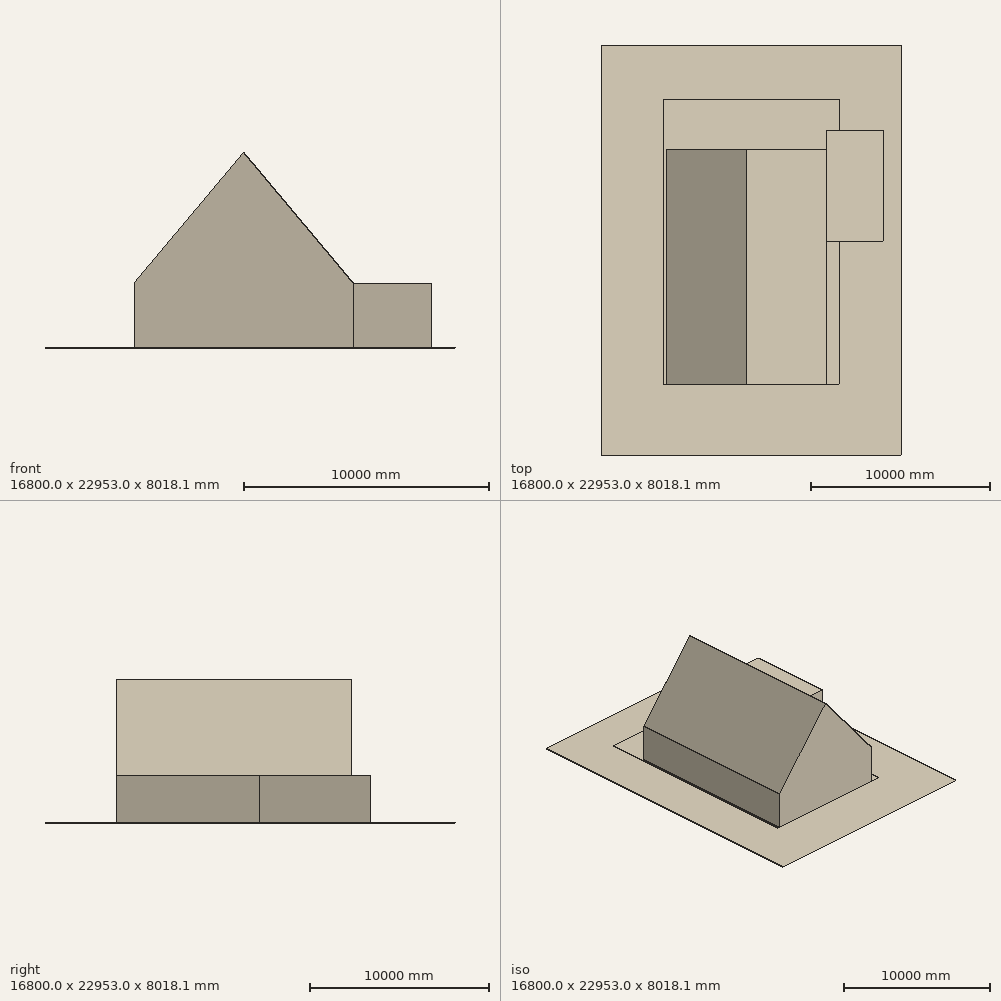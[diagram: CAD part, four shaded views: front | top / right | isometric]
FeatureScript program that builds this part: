
annotation { "Feature Type Name" : "Feature", "Feature Type Description" : "" }
export const myFeature = defineFeature(function(context is Context, id is Id, definition is map)
    precondition{}
    {
        {
            var Q0;
            Q0=qCreatedBy(makeId("Top.planeOp"),FACE);
            var sketch = newSketch(context, id + "F0", { "sketchPlane" : qUnion([Q0])});
            skLineSegment(sketch, "E0.bottom", {"start": v(-5071.58, -11461.11) * mm, "end": v(11728.42, -11461.11) * mm});
            skLineSegment(sketch, "E0.top", {"start": v(-5071.58, 11491.89) * mm, "end": v(11728.42, 11491.89) * mm});
            skLineSegment(sketch, "E0.left", {"start": v(-5071.58, -11461.11) * mm, "end": v(-5071.58, 11491.89) * mm});
            skLineSegment(sketch, "E0.right", {"start": v(11728.42, -11461.11) * mm, "end": v(11728.42, 11491.89) * mm});
            skSolve(sketch);
        }
        {
            var Q0;
            Q0=makeQuery(id+"F0.imprint","IMPRINT",FACE,{"disambiguationData":[TD([[makeQuery(id+"F0.imprint","IMPRINT",EDGE,{"derivedFrom":sQuery(id+"F0.wireOp",EDGE,"E0.bottom")}),1.0]])]});
            extrude(context, id + "F1", {"entities" : qUnion([Q0]), "depth" : 25 * mm, "offsetDistance" : 25 * mm});
        }
        {
            var Q0;
            Q0=makeQuery(id+"F1.opExtrude","CAP_FACE",FACE,{"disambiguationData":[OSD([sQuery(id+"F0.wireOp",EDGE,"E0.bottom"),sQuery(id+"F0.wireOp",EDGE,"E0.top"),sQuery(id+"F0.wireOp",EDGE,"E0.left"),sQuery(id+"F0.wireOp",EDGE,"E0.right")])],"isStart":false});
            var sketch = newSketch(context, id + "F2", { "sketchPlane" : qUnion([Q0])});
            skLineSegment(sketch, "E1.bottom", {"start": v(-1571.58, 8491.89) * mm, "end": v(8228.42, 8491.89) * mm});
            skLineSegment(sketch, "E1.top", {"start": v(-1571.58, -7461.11) * mm, "end": v(8228.42, -7461.11) * mm});
            skLineSegment(sketch, "E1.left", {"start": v(-1571.58, 8491.89) * mm, "end": v(-1571.58, -7461.11) * mm});
            skLineSegment(sketch, "E1.right", {"start": v(8228.42, 8491.89) * mm, "end": v(8228.42, -7461.11) * mm});
            skSolve(sketch);
        }
        {
            var Q0;
            Q0=qSketchRegion(id+"F2",true);
            extrude(context, id + "F3", {"entities" : qUnion([Q0]), "operationType" : NewBodyOperationType.ADD, "depth" : 10 * mm, "offsetDistance" : 25 * mm});
        }
        {
            var Q0;
            Q0=makeQuery(id+"F1.opExtrude","CAP_FACE",FACE,{"disambiguationData":[OSD([sQuery(id+"F0.wireOp",EDGE,"E0.bottom"),sQuery(id+"F0.wireOp",EDGE,"E0.top"),sQuery(id+"F0.wireOp",EDGE,"E0.left"),sQuery(id+"F0.wireOp",EDGE,"E0.right")])],"isStart":false});
            var sketch = newSketch(context, id + "F4", { "sketchPlane" : qUnion([Q0])});
            skLineSegment(sketch, "E2.bottom", {"start": v(-1571.58, 8491.89) * mm, "end": v(-4071.58, 8491.89) * mm});
            skLineSegment(sketch, "E2.top", {"start": v(-1571.58, -6461.11) * mm, "end": v(-4071.58, -6461.11) * mm});
            skLineSegment(sketch, "E2.left", {"start": v(-1571.58, 8491.89) * mm, "end": v(-1571.58, -6461.11) * mm});
            skLineSegment(sketch, "E2.right", {"start": v(-4071.58, 8491.89) * mm, "end": v(-4071.58, -6461.11) * mm});
            skLineSegment(sketch, "E3.bottom", {"start": v(8228.42, 8491.89) * mm, "end": v(10728.42, 8491.89) * mm});
            skLineSegment(sketch, "E3.top", {"start": v(8228.42, -4461.11) * mm, "end": v(10728.42, -4461.11) * mm});
            skLineSegment(sketch, "E3.left", {"start": v(8228.42, 8491.89) * mm, "end": v(8228.42, -4461.11) * mm});
            skLineSegment(sketch, "E3.right", {"start": v(10728.42, 8491.89) * mm, "end": v(10728.42, -4461.11) * mm});
            skSolve(sketch);
        }
        {
            var Q0;
            Q0=makeQuery(id+"F3.opExtrude","CAP_FACE",FACE,{"disambiguationData":[OSD([sQuery(id+"F2.wireOp",EDGE,"E1.bottom"),sQuery(id+"F2.wireOp",EDGE,"E1.top"),sQuery(id+"F2.wireOp",EDGE,"E1.left"),sQuery(id+"F2.wireOp",EDGE,"E1.right")])],"isStart":false});
            var sketch = newSketch(context, id + "F5", { "sketchPlane" : qUnion([Q0])});
            skLineSegment(sketch, "E4.bottom", {"start": v(7528.42, -7461.11) * mm, "end": v(-1421.58, -7461.11) * mm});
            skLineSegment(sketch, "E4.top", {"start": v(7528.42, 5688.89) * mm, "end": v(-1421.58, 5688.89) * mm});
            skLineSegment(sketch, "E4.left", {"start": v(7528.42, -7461.11) * mm, "end": v(7528.42, 5688.89) * mm});
            skLineSegment(sketch, "E4.right", {"start": v(-1421.58, -7461.11) * mm, "end": v(-1421.58, 5688.89) * mm});
            skSolve(sketch);
        }
        {
            var Q0;
            Q0 = qSketchRegion(id + "F5", true);
            extrude(context, id + "F6", {"entities" : qUnion([Q0]), "operationType" : NewBodyOperationType.ADD, "depth" : 2650 * mm, "offsetDistance" : 25 * mm});
        }
        {
            var Q0;
            Q0=makeQuery(id+"F6.boolean.opBoolean","MERGE",FACE,{"derivedFrom":[makeQuery(id+"F3.opExtrude","SWEPT_FACE",FACE,{"disambiguationData":[OSD([sQuery(id+"F2.wireOp",EDGE,"E1.top")])]}),makeQuery(id+"F6.opExtrude","SWEPT_FACE",FACE,{"disambiguationData":[OSD([sQuery(id+"F5.wireOp",EDGE,"E4.bottom")])]})]});
            var sketch = newSketch(context, id + "F7", { "sketchPlane" : qUnion([Q0])});
            skLineSegment(sketch, "E5", {"start": v(-1421.58, 2685) * mm, "end": v(3053.42, 8018.1) * mm});
            skLineSegment(sketch, "E6", {"start": v(3053.42, 8018.1) * mm, "end": v(7528.42, 2685) * mm});
            skLineSegment(sketch, "E7", {"start": v(7528.42, 2685) * mm, "end": v(-1421.58, 2685) * mm});
            skSolve(sketch);
        }
        {
            var Q0;
            Q0 = qSketchRegion(id + "F7", true);
            var Q1;
            Q1=makeQuery(id+"F6.opExtrude","SWEPT_FACE",FACE,{"disambiguationData":[OSD([sQuery(id+"F5.wireOp",EDGE,"E4.top")])]});
            extrude(context, id + "F8", {"entities" : qUnion([Q0]), "operationType" : NewBodyOperationType.ADD, "endBound" : BoundingType.UP_TO_SURFACE, "oppositeDirection" : true, "depth" : 6260 * mm, "endBoundEntityFace" : qUnion([Q1]), "offsetDistance" : 25 * mm});
        }
        {
            var Q0;
            Q0=makeQuery(id+"F4.imprint","IMPRINT",FACE,{"disambiguationData":[TD([[makeQuery(id+"F4.imprint","IMPRINT",EDGE,{"derivedFrom":sQuery(id+"F4.wireOp",EDGE,"E2.bottom")}),-1.0]])]});
            var sketch = newSketch(context, id + "F9", { "sketchPlane" : qUnion([Q0])});
            skLineSegment(sketch, "E8.bottom", {"start": v(10728.42, 6738.89) * mm, "end": v(7528.42, 6738.89) * mm});
            skLineSegment(sketch, "E8.top", {"start": v(10728.42, 538.89) * mm, "end": v(7528.42, 538.89) * mm});
            skLineSegment(sketch, "E8.left", {"start": v(10728.42, 6738.89) * mm, "end": v(10728.42, 538.89) * mm});
            skLineSegment(sketch, "E8.right", {"start": v(7528.42, 6738.89) * mm, "end": v(7528.42, 538.89) * mm});
            skSolve(sketch);
        }
        {
            var Q0;
            Q0 = qSketchRegion(id + "F9", true);
            extrude(context, id + "F10", {"entities" : qUnion([Q0]), "operationType" : NewBodyOperationType.ADD, "depth" : 2650 * mm, "offsetDistance" : 25 * mm});
        }
    });
